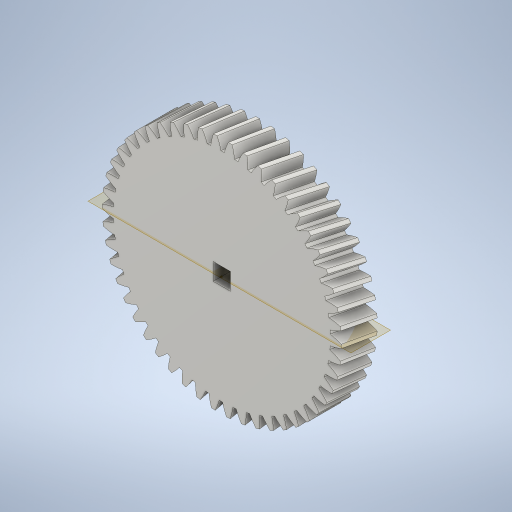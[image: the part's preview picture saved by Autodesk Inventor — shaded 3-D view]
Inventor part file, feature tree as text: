
AUTODESK INVENTOR PART (.ipt)
format: ipt  version: 2023.2 (Build 272271030, 271C)  size: 873,984 bytes
history: native  units: mm (DEFAULTED — no unit token found)
features: plane x5, other x4, sketch x4, extrude x3
ambient origin geometry x8: Origin, YZ Plane, XZ Plane, XY Plane, X Axis, Y Axis, Z Axis, Center Point
bodies: Solid1 (feature_tree)
feature tree (16):
  extrude  "Extrusion1"  Depth=10.0mm TaperAngle=0.0deg
  plane  "Work Plane1"
  plane  "Work Plane2"
  plane  "Work Plane3"
  other  "Spur Gear"
  extrude  "Extrusion2"  Depth=76.2mm TaperAngle=0.0deg
  other  "Work Point2"
  sketch  "Sketch4"  dims[d14=0.0mm d15=42.556529mm d16=0.0mm d17=0.0mm d18=0.0mm d19=42.556529mm d20=6.75mm d21=25.4mm d22=0.0mm d23=2.0mm d24=2.0mm d25=2.0mm d27=3.0mm d28=25.4mm d29=0.0mm d30=2.0mm]
  plane  "Work Plane7"
  extrude  "Extrusion3"  TaperAngle=0.0deg  [1 undecoded]
  sketch  "Sketch1"  dims[d0=66.51159mm d1=10.0mm d2=0.0mm]
  sketch  "Sketch2"  dims[d3=64.47959mm d4=76.2mm d5=0.0mm]
  other  "Srf1"
  sketch  "Sketch3"  dims[d6=0.0mm d7=0.628319mm d9=0.0mm]
  plane  "Work Plane4"
  other  "Pitch Diameter"
note: 1 required parameter value undecoded (feature->parameter linkage not recoverable at this tier; creation-order binding heuristic only, values carry confidence <= 0.55)
